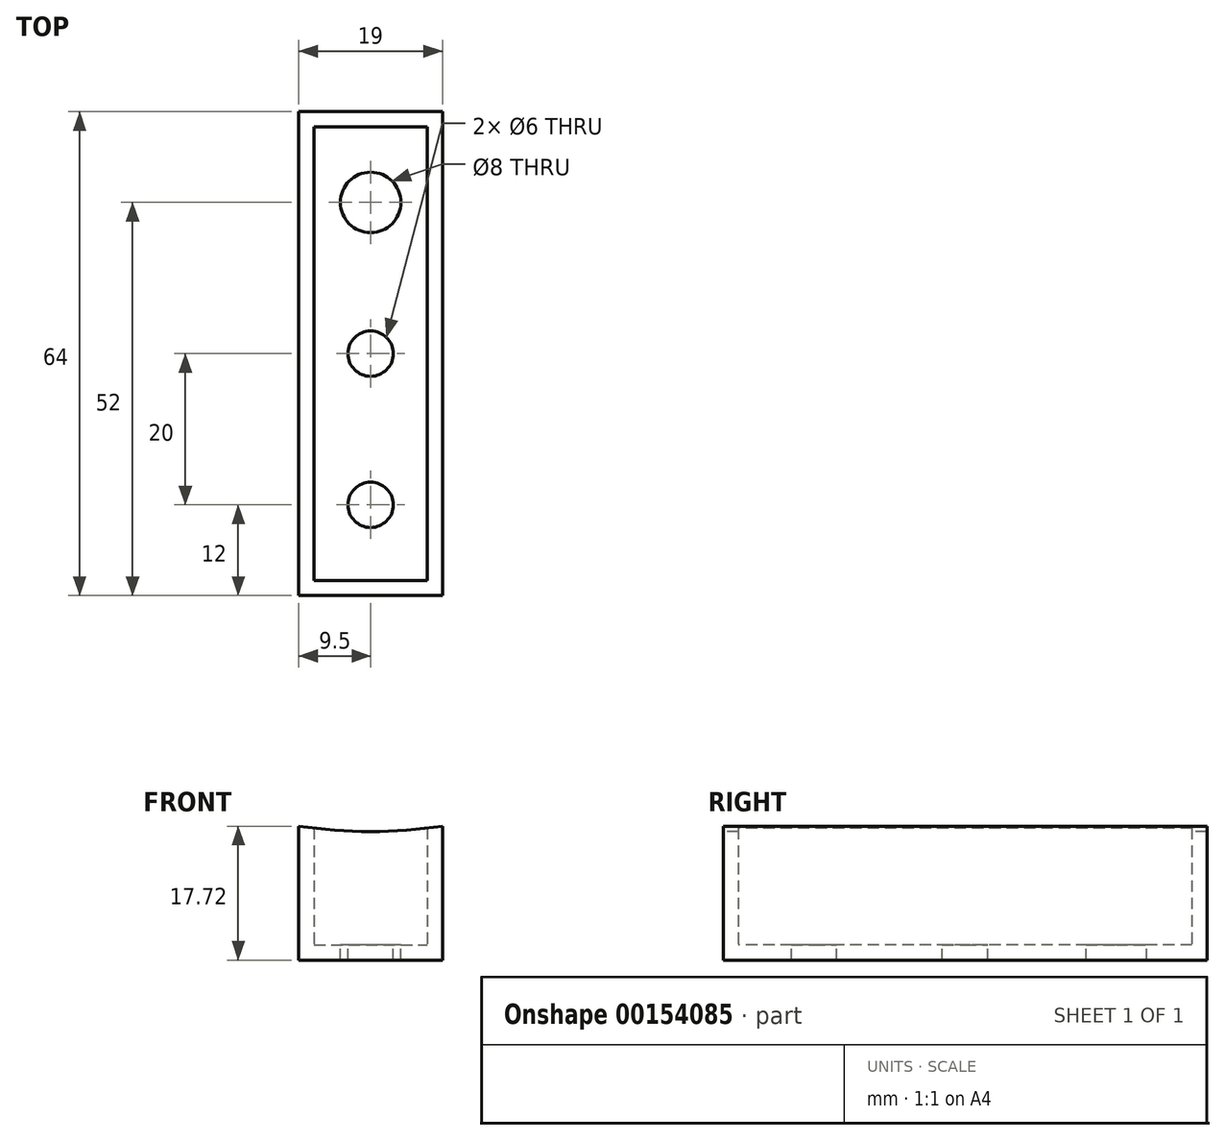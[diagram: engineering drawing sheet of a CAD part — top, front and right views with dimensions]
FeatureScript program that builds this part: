
annotation { "Feature Type Name" : "Feature", "Feature Type Description" : "" }
export const myFeature = defineFeature(function(context is Context, id is Id, definition is map)
    precondition{}
    {
        {
            var Q0;
            Q0=qCreatedBy(makeId("Front.planeOp"),FACE);
            var sketch = newSketch(context, id + "F0", { "sketchPlane" : qUnion([Q0])});
            skLineSegment(sketch, "E0", {"start": v(-9.5, 0) * mm, "end": v(9.5, 0) * mm});
            skArc(sketch, "E1", {"start": v(-9.5, 17.72) * mm, "mid": v(0, 17) * mm, "end": v(9.5, 17.72) * mm});
            skLineSegment(sketch, "E2", {"start": v(-9.5, 0) * mm, "end": v(-9.5, 17.72) * mm});
            skLineSegment(sketch, "E3", {"start": v(9.5, 0) * mm, "end": v(9.5, 17.72) * mm});
            skSolve(sketch);
        }
        {
            var Q0;
            Q0=makeQuery(id+"F0.imprint","IMPRINT",FACE,{"disambiguationData":[TD([[makeQuery(id+"F0.imprint","IMPRINT",EDGE,{"derivedFrom":sQuery(id+"F0.wireOp",EDGE,"E0")}),1.0]])]});
            extrude(context, id + "F1", {"entities" : qUnion([Q0]), "oppositeDirection" : true, "depth" : 64 * mm});
        }
        {
            var Q0;
            Q0=qCreatedBy(makeId("Top.planeOp"),FACE);
            cPlane(context, id + "F2", {"entities" : qUnion([Q0]), "cplaneType" : CPlaneType.OFFSET, "offset" : 2 * mm, "width" : 150 * mm, "height" : 150 * mm});
        }
        {
            var Q0;
            Q0=qCreatedBy(id+"F2.planeOp",FACE);
            var sketch = newSketch(context, id + "F3", { "sketchPlane" : qUnion([Q0])});
            skLineSegment(sketch, "E4.bottom", {"start": v(-7.5, 62) * mm, "end": v(7.5, 62) * mm});
            skLineSegment(sketch, "E4.top", {"start": v(-7.5, 2) * mm, "end": v(7.5, 2) * mm});
            skLineSegment(sketch, "E4.left", {"start": v(-7.5, 62) * mm, "end": v(-7.5, 2) * mm});
            skLineSegment(sketch, "E4.right", {"start": v(7.5, 62) * mm, "end": v(7.5, 2) * mm});
            skSolve(sketch);
        }
        {
            var Q0;
            Q0 = qSketchRegion(id + "F3", true);
            extrude(context, id + "F4", {"entities" : qUnion([Q0]), "operationType" : NewBodyOperationType.REMOVE, "depth" : 25 * mm});
        }
        {
            var Q0;
            Q0=makeQuery(id+"F4.boolean.opBoolean","COPY",FACE,{"derivedFrom":makeQuery(id+"F4.opExtrude","CAP_FACE",FACE,{"disambiguationData":[OSD([sQuery(id+"F3.wireOp",EDGE,"E4.bottom"),sQuery(id+"F3.wireOp",EDGE,"E4.top"),sQuery(id+"F3.wireOp",EDGE,"E4.left"),sQuery(id+"F3.wireOp",EDGE,"E4.right")])],"isStart":true})});
            var sketch = newSketch(context, id + "F5", { "sketchPlane" : qUnion([Q0])});
            skCircle(sketch, "E5", {"center": v(0, 12) * mm, "radius": 3 * mm});
            skCircle(sketch, "E6", {"center": v(0, 32) * mm, "radius": 3 * mm});
            skCircle(sketch, "E7", {"center": v(0, 52) * mm, "radius": 4 * mm});
            skSolve(sketch);
        }
        {
            var Q0;
            Q0=makeQuery(id+"F5.imprint","IMPRINT",FACE,{"disambiguationData":[TD([[makeQuery(id+"F5.imprint","IMPRINT",EDGE,{"derivedFrom":sQuery(id+"F5.wireOp",EDGE,"E5")}),1.0]])]});
            var Q1;
            Q1=makeQuery(id+"F5.imprint","IMPRINT",FACE,{"disambiguationData":[TD([[makeQuery(id+"F5.imprint","IMPRINT",EDGE,{"derivedFrom":sQuery(id+"F5.wireOp",EDGE,"E6")}),1.0]])]});
            var Q2;
            Q2=makeQuery(id+"F5.imprint","IMPRINT",FACE,{"disambiguationData":[TD([[makeQuery(id+"F5.imprint","IMPRINT",EDGE,{"derivedFrom":sQuery(id+"F5.wireOp",EDGE,"E7")}),1.0]])]});
            extrude(context, id + "F6", {"entities" : qUnion([Q0, Q1, Q2]), "operationType" : NewBodyOperationType.REMOVE, "oppositeDirection" : true, "depth" : 25 * mm});
        }
    });
